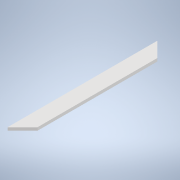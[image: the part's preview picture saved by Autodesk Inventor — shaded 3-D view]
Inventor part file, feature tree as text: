
AUTODESK INVENTOR PART (.ipt)
format: ipt  version: 2020 (Build 240168000, 168)  size: 96,768 bytes
history: native  units: mm
features: extrude x1, sketch x1
ambient origin geometry x8: Origin, YZ Plane, XZ Plane, XY Plane, X Axis, Y Axis, Z Axis, Center Point
bodies: Solid1 (feature_tree)
feature tree (2):
  extrude  "Extrusion1"  Depth=5.0mm
  sketch  "Sketch1"  dims[d0=45.0deg d1=5.0mm d2=45.0deg d4=1.0mm d5=0.0mm d6=40.0mm]
